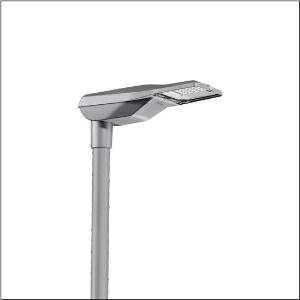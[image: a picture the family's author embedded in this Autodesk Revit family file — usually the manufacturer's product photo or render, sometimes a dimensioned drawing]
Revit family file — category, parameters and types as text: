
# Revit family: streetlight_sl_21_iq_micro___st1_0a_5xe1d31g08cb_12bc
name_source: partatom
category: Lighting Fixtures
units: mm (PartAtom-declared; Revit-internal decimal feet)

## family parameters
Cut with Voids When Loaded = No
Host = Face
Light Source = No
Part Type = Normal
Room Calculation Point = No
Round Connector Dimension = Use Diameter
Shared = No

## types (1)
- --- (1 x LED, 2870 lm, 19.4 W, 3000K)
    Apparent Load = 19 VA
    CIE Flux Codes = 37 72 97 100 100
    Color Rendering = 70
    Color Temperature = 3000K
    Default Elevation = 1800 mm
    Description = Streetlight SL 21 iQ micro, mast luminaire, primary light control with lens, of PMMA, primary optical cover: cover, of toughened safety glass, transparent, light distribution: ST1.0a, light emission: direct distribution, primary light characteristic: asymmetric, installation type: post-top, side-entry, LED, High Power LED, rated luminous flux: 2.870lm, luminous efficacy: 148lm/W, light colour: 730, colour temperature: 3000K, control: Street-Remote, Auto-Match, Temp-Guard, Lumen-Switch, Night-Set, Smart-Wire, Light-Fading, Desk-Remote (wireless, voltage-free reading and setting of iQ features in the workshop via application-optimized NFC function/RFID function), optimised constant luminous flux control (CLO 2.0), presetting dimming linear, mains connection: 220..240V, AC, 50/60Hz, start of lifetime: 19W, end of service life: 20W, reduction: 10W, luminaire housing, of diecast aluminium, powder-coated, Siteco® metallic grey (DB 702S), corrosivity category C5 mid according to DIN EN ISO 12944, please order mast flange separately, inclination adjustable: 0°, 5°, 10°, 15°, sealing non-destructively replaceable, multi-level sealing system, length: 528mm, width: 235mm, height: 110mm, mast flange for spigot size: 42mm (side-entry): 5XC10008XM4, 60/48mm (side-entry/post-top): 5XC10108XM2, 76/60mm (side-entry/post-top): 5XC10108XM1, protection rating (complete): IP66, insulation class (complete): insulation class II (safety insulation), certification: CE, ENEC, ENEC+, VDE, impact resistance: IK09, permissible operating ambient temperature for outdoor applications: -40..+50°C, standard-compliant lighting for roads and squares, packaging unit: 1 piece

Light Distribution: ST1.0a
    Height = 110 mm
    Lamp = 1 x LED
    Lamp Light Flux = 2870 lm
    Lamp Power = 19.4 W
    Lamp count = 1
    Length = 528 mm
    Luminous efficacy = 148 lm/W
    Manufacturer = Siteco
    ModVariant = No
    Model = 5XE1D31G08CB
    Number of Poles = 1
    OnlyDefault = Yes
    Power Factor = 1
    Product Name = Streetlight SL 21 iQ micro | ST1.0a
    Product group = mast luminaire | pylon top
    ProductGroupID = 6100
    Protection Class = Protection class II
    Protection Degree = IP 66
    RLX_Detail_Level = 1
    RLX_Emergency_Light_Flux = 0 lm
    RLX_Emergency_Type = 0
    RLX_Emergency_Type_DB = No
    RlxData = <blob elided: 98833 chars, md5=788cc9a8>
    Socket = socket
    Standby Power = 0 W
    System Light Flux = 2870 lm
    System Power = 19 W
    Type Comments = factory setting: luminous flux: 100 % | dim-lin: 254 | 387 mA
    Type Image = l_1006881.jpg
    URL = http://relux.com
    VarID = @adj_070577
    Voltage = 0 V
    Weight = 0.00 kg
    Width = 235 mm

## geometry (parser evidence)
native form markers: Blend x4, Sweep x10
no freeform markers — native parametric forms only
